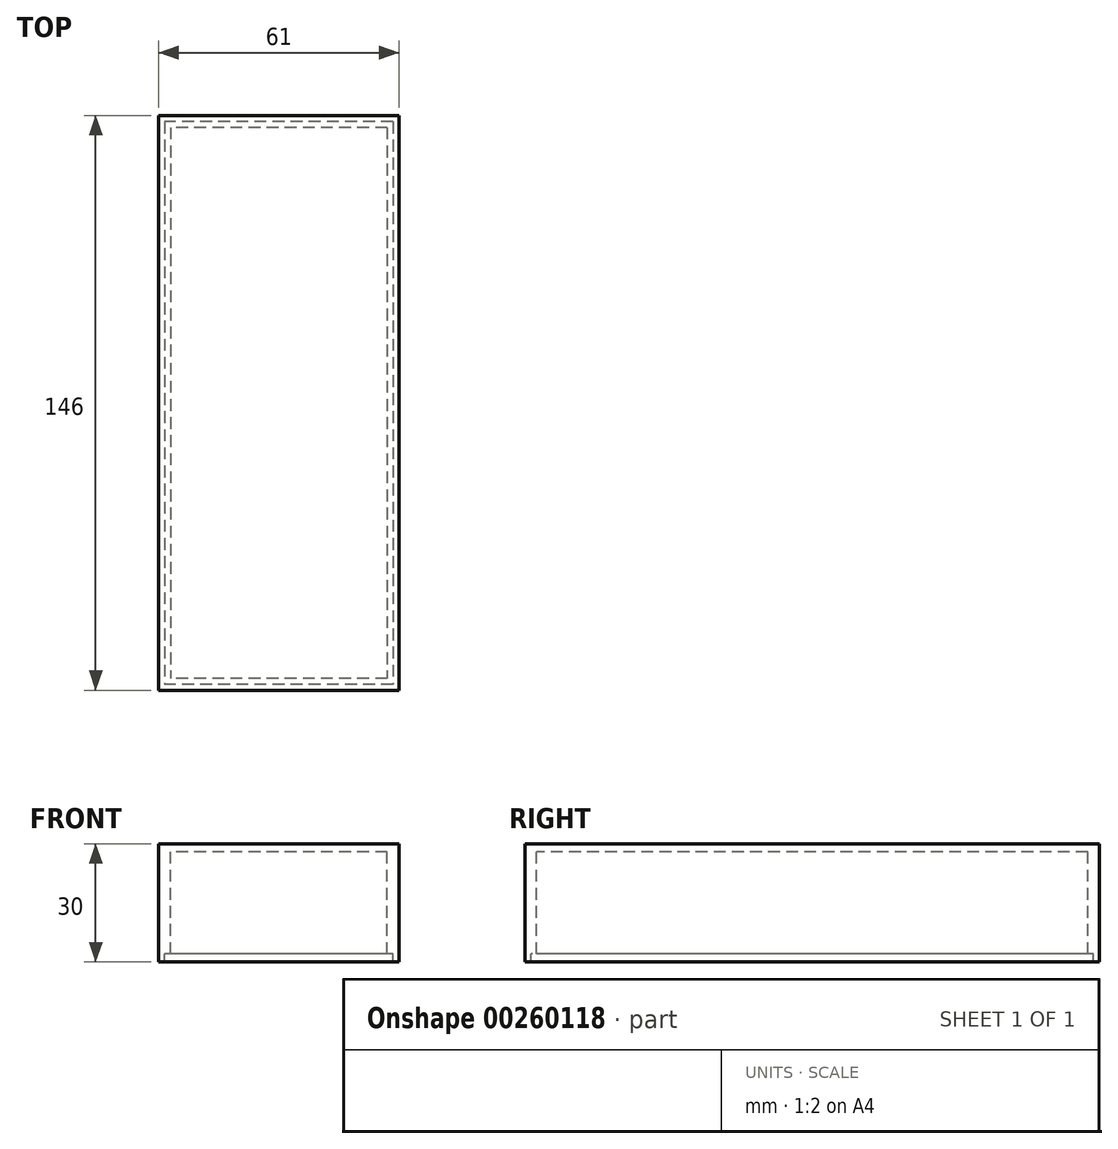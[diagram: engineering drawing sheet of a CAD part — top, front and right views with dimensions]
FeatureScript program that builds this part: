
annotation { "Feature Type Name" : "Feature", "Feature Type Description" : "" }
export const myFeature = defineFeature(function(context is Context, id is Id, definition is map)
    precondition{}
    {
        {
            var Q0;
            Q0=qCreatedBy(makeId("Top.planeOp"),FACE);
            var sketch = newSketch(context, id + "F0", { "sketchPlane" : qUnion([Q0])});
            skLineSegment(sketch, "E0.bottom", {"start": v(27.5, 70) * mm, "end": v(-27.5, 70) * mm});
            skLineSegment(sketch, "E0.top", {"start": v(27.5, -70) * mm, "end": v(-27.5, -70) * mm});
            skLineSegment(sketch, "E0.left", {"start": v(27.5, 70) * mm, "end": v(27.5, -70) * mm});
            skLineSegment(sketch, "E0.right", {"start": v(-27.5, 70) * mm, "end": v(-27.5, -70) * mm});
            skPoint(sketch, "E0.middle", {"position": v(0, 0) * mm});
            skLineSegment(sketch, "E1.bottom", {"start": v(29, 71.5) * mm, "end": v(-29, 71.5) * mm});
            skLineSegment(sketch, "E1.top", {"start": v(29, -71.5) * mm, "end": v(-29, -71.5) * mm});
            skLineSegment(sketch, "E1.left", {"start": v(29, 71.5) * mm, "end": v(29, -71.5) * mm});
            skLineSegment(sketch, "E1.right", {"start": v(-29, 71.5) * mm, "end": v(-29, -71.5) * mm});
            skLineSegment(sketch, "E2.bottom", {"start": v(30.5, 73) * mm, "end": v(-30.5, 73) * mm});
            skLineSegment(sketch, "E2.top", {"start": v(30.5, -73) * mm, "end": v(-30.5, -73) * mm});
            skLineSegment(sketch, "E2.left", {"start": v(30.5, 73) * mm, "end": v(30.5, -73) * mm});
            skLineSegment(sketch, "E2.right", {"start": v(-30.5, 73) * mm, "end": v(-30.5, -73) * mm});
            skSolve(sketch);
        }
        {
            var Q0;
            Q0=makeQuery(id+"F0.imprint","IMPRINT",FACE,{"disambiguationData":[TD([[makeQuery(id+"F0.imprint","IMPRINT",EDGE,{"derivedFrom":sQuery(id+"F0.wireOp",EDGE,"E0.bottom")}),1.0]])]});
            var Q1;
            Q1=makeQuery(id+"F0.imprint","IMPRINT",FACE,{"disambiguationData":[TD([[makeQuery(id+"F0.imprint","IMPRINT",EDGE,{"derivedFrom":sQuery(id+"F0.wireOp",EDGE,"E0.bottom")}),-1.0]])]});
            var Q2;
            Q2=makeQuery(id+"F0.imprint","IMPRINT",FACE,{"disambiguationData":[TD([[makeQuery(id+"F0.imprint","IMPRINT",EDGE,{"derivedFrom":sQuery(id+"F0.wireOp",EDGE,"E1.bottom")}),-1.0]])]});
            extrude(context, id + "F1", {"entities" : qUnion([Q0, Q1, Q2]), "oppositeDirection" : true, "depth" : 2 * mm});
        }
        {
            var Q0;
            Q0=makeQuery(id+"F0.imprint","IMPRINT",FACE,{"disambiguationData":[TD([[makeQuery(id+"F0.imprint","IMPRINT",EDGE,{"derivedFrom":sQuery(id+"F0.wireOp",EDGE,"E0.bottom")}),-1.0]])]});
            var Q1;
            Q1=makeQuery(id+"F0.imprint","IMPRINT",FACE,{"disambiguationData":[TD([[makeQuery(id+"F0.imprint","IMPRINT",EDGE,{"derivedFrom":sQuery(id+"F0.wireOp",EDGE,"E1.bottom")}),-1.0]])]});
            extrude(context, id + "F2", {"entities" : qUnion([Q0, Q1]), "operationType" : NewBodyOperationType.ADD, "oppositeDirection" : true, "depth" : 28 * mm});
        }
        {
            var Q0;
            Q0=makeQuery(id+"F0.imprint","IMPRINT",FACE,{"disambiguationData":[TD([[makeQuery(id+"F0.imprint","IMPRINT",EDGE,{"derivedFrom":sQuery(id+"F0.wireOp",EDGE,"E1.bottom")}),-1.0]])]});
            extrude(context, id + "F3", {"entities" : qUnion([Q0]), "operationType" : NewBodyOperationType.ADD, "oppositeDirection" : true, "depth" : 30 * mm});
        }
    });
